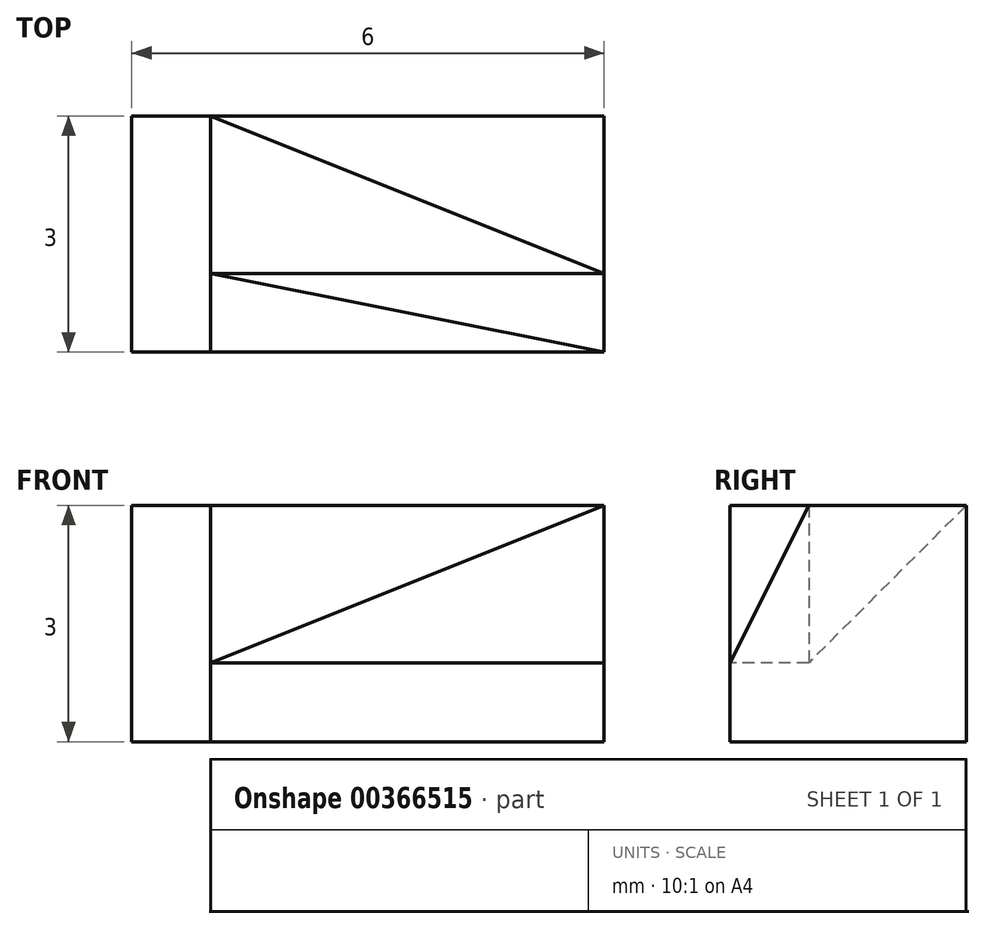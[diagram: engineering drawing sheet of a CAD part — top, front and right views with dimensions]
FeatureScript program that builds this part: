
annotation { "Feature Type Name" : "Feature", "Feature Type Description" : "" }
export const myFeature = defineFeature(function(context is Context, id is Id, definition is map)
    precondition{}
    {
        {
            var Q0;
            Q0=qCreatedBy(makeId("Top.planeOp"),FACE);
            var sketch = newSketch(context, id + "F0", { "sketchPlane" : qUnion([Q0])});
            skLineSegment(sketch, "E0", {"start": v(0, 0) * mm, "end": v(5, 0) * mm});
            skLineSegment(sketch, "E1", {"start": v(5, 0) * mm, "end": v(5, 3) * mm});
            skLineSegment(sketch, "E2", {"start": v(5, 3) * mm, "end": v(0, 3) * mm});
            skLineSegment(sketch, "E3", {"start": v(0, 3) * mm, "end": v(0, 0) * mm});
            skSolve(sketch);
        }
        {
            var Q0;
            Q0=qSketchRegion(id+"F0",true);
            extrude(context, id + "F1", {"entities" : qUnion([Q0]), "depth" : 3 * mm});
        }
        {
            var Q0;
            Q0=makeQuery(id+"F1.opExtrude","CAP_FACE",FACE,{"disambiguationData":[OSD([sQuery(id+"F0.wireOp",EDGE,"E0"),sQuery(id+"F0.wireOp",EDGE,"E1"),sQuery(id+"F0.wireOp",EDGE,"E2"),sQuery(id+"F0.wireOp",EDGE,"E3")])],"isStart":false});
            var sketch = newSketch(context, id + "F2", { "sketchPlane" : qUnion([Q0])});
            skLineSegment(sketch, "E4", {"start": v(0, 0) * mm, "end": v(0, 1) * mm});
            skLineSegment(sketch, "E5", {"start": v(0, 1) * mm, "end": v(5, 0) * mm});
            skSolve(sketch);
        }
        {
            var Q0;
            Q0=makeQuery(id+"F2.imprint","IMPRINT",FACE,{"disambiguationData":[TD([[makeQuery(id+"F2.imprint","IMPRINT",EDGE,{"derivedFrom":sQuery(id+"F2.wireOp",EDGE,"E4")}),1.0]])]});
            extrude(context, id + "F3", {"entities" : qUnion([Q0]), "operationType" : NewBodyOperationType.REMOVE, "oppositeDirection" : true, "depth" : 2 * mm});
        }
        {
            var Q0;
            Q0=makeQuery(id+"F1.opExtrude","SWEPT_FACE",FACE,{"disambiguationData":[OSD([sQuery(id+"F0.wireOp",EDGE,"E1")])]});
            var sketch = newSketch(context, id + "F4", { "sketchPlane" : qUnion([Q0])});
            skLineSegment(sketch, "E6", {"start": v(0, 0) * mm, "end": v(1, 0) * mm});
            skLineSegment(sketch, "E7", {"start": v(1, 0) * mm, "end": v(1, 3) * mm});
            skSolve(sketch);
        }
        {
            var Q0;
            Q0=sQuery(id+"F4.wireOp",VERTEX,"E7.end");
            var Q1;
            Q1=makeQuery(id+"F3.boolean.opBoolean","COPY",VERTEX,{"derivedFrom":makeQuery(id+"F3.opExtrude","CAP_VERTEX",VERTEX,{"disambiguationData":[OSD([sQuery(id+"F0.wireOp",EDGE,"E0"),sQuery(id+"F0.wireOp",EDGE,"E1"),sQuery(id+"F2.wireOp",EDGE,"E5")])],"isStart":false})});
            var Q2;
            Q2=makeQuery(id+"F3.boolean.opBoolean","COPY",VERTEX,{"derivedFrom":makeQuery(id+"F3.opExtrude","CAP_VERTEX",VERTEX,{"disambiguationData":[OSD([sQuery(id+"F0.wireOp",EDGE,"E3"),sQuery(id+"F2.wireOp",EDGE,"E4"),sQuery(id+"F2.wireOp",EDGE,"E5")])],"isStart":false})});
            cPlane(context, id + "F5", {"entities" : qUnion([Q0, Q1, Q2]), "cplaneType" : CPlaneType.THREE_POINT, "offset" : 25 * mm, "width" : 150 * mm, "height" : 150 * mm});
        }
        {
            var Q0;
            Q0=qCreatedBy(id+"F5.planeOp",FACE);
            var sketch = newSketch(context, id + "F6", { "sketchPlane" : qUnion([Q0])});
            skPoint(sketch, "E8.0", {"position": v(-0.08, 1.34) * mm});
            skPoint(sketch, "E9.0", {"position": v(5, 3.13) * mm});
            skPoint(sketch, "E10.0", {"position": v(5, 0.9) * mm});
            skLineSegment(sketch, "E11", {"start": v(-0.08, 1.34) * mm, "end": v(5, 0.9) * mm});
            skLineSegment(sketch, "E12", {"start": v(5, 3.13) * mm, "end": v(5, 0.9) * mm});
            skLineSegment(sketch, "E13", {"start": v(5, 3.13) * mm, "end": v(-0.08, 1.34) * mm});
            skLineSegment(sketch, "E14", {"start": v(5, 3.13) * mm, "end": v(6.74, 3.13) * mm});
            skLineSegment(sketch, "E15", {"start": v(6.74, 3.13) * mm, "end": v(6.74, 0.9) * mm});
            skLineSegment(sketch, "E16", {"start": v(6.74, 0.9) * mm, "end": v(5, 0.9) * mm});
            skSolve(sketch);
        }
        {
            var Q0;
            Q0=qSketchRegion(id+"F6",true);
            extrude(context, id + "F7", {"entities" : qUnion([Q0]), "operationType" : NewBodyOperationType.REMOVE, "depth" : 25 * mm});
        }
        {
            var Q0;
            Q0=makeQuery(id+"F1.opExtrude","CAP_VERTEX",VERTEX,{"disambiguationData":[OSD([sQuery(id+"F0.wireOp",EDGE,"E2"),sQuery(id+"F0.wireOp",EDGE,"E3")])],"isStart":false});
            var Q1;
            Q1=makeQuery(id+"F7.boolean.opBoolean","MERGE",VERTEX,{"derivedFrom":[makeQuery(id+"F3.boolean.opBoolean","COPY",VERTEX,{"derivedFrom":makeQuery(id+"F3.opExtrude","CAP_VERTEX",VERTEX,{"disambiguationData":[OSD([sQuery(id+"F0.wireOp",EDGE,"E3"),sQuery(id+"F2.wireOp",EDGE,"E4"),sQuery(id+"F2.wireOp",EDGE,"E5")])],"isStart":false})}),makeQuery(id+"F7.opExtrude","CAP_VERTEX",VERTEX,{"disambiguationData":[OSD([sQuery(id+"F6.wireOp",EDGE,"E11"),sQuery(id+"F6.wireOp",EDGE,"E13")])],"isStart":true})]});
            var Q2;
            Q2=sQuery(id+"F4.wireOp",VERTEX,"E7.end");
            cPlane(context, id + "F8", {"entities" : qUnion([Q0, Q1, Q2]), "cplaneType" : CPlaneType.THREE_POINT, "offset" : 25 * mm, "width" : 150 * mm, "height" : 150 * mm});
        }
        {
            var Q0;
            Q0=qCreatedBy(id+"F8.planeOp",FACE);
            var sketch = newSketch(context, id + "F9", { "sketchPlane" : qUnion([Q0])});
            skPoint(sketch, "E17.0", {"position": v(0, 4.24) * mm});
            skPoint(sketch, "E17.1", {"position": v(0, 1.41) * mm});
            skPoint(sketch, "E17.2", {"position": v(-5.2, 2.83) * mm});
            skLineSegment(sketch, "E18", {"start": v(0, 4.24) * mm, "end": v(0, 1.41) * mm});
            skLineSegment(sketch, "E19", {"start": v(-5.2, 2.83) * mm, "end": v(0, 4.24) * mm});
            skLineSegment(sketch, "E20", {"start": v(-5.2, 2.83) * mm, "end": v(0, 1.41) * mm});
            skLineSegment(sketch, "E21", {"start": v(-5.2, 2.83) * mm, "end": v(-5.2, 1.5) * mm});
            skLineSegment(sketch, "E22", {"start": v(-5.2, 1.5) * mm, "end": v(0, 1.41) * mm});
            skSolve(sketch);
        }
        {
            var Q0;
            Q0=qSketchRegion(id+"F9",true);
            extrude(context, id + "F10", {"entities" : qUnion([Q0]), "operationType" : NewBodyOperationType.REMOVE, "oppositeDirection" : true, "depth" : 25 * mm});
        }
        {
            var Q0;
            Q0=qCreatedBy(makeId("Front.planeOp"),FACE);
            var sketch = newSketch(context, id + "F11", { "sketchPlane" : qUnion([Q0])});
            skLineSegment(sketch, "E23", {"start": v(0, 0) * mm, "end": v(-1, 0) * mm});
            skLineSegment(sketch, "E24", {"start": v(-1, 0) * mm, "end": v(-1, 3) * mm});
            skLineSegment(sketch, "E25", {"start": v(-1, 3) * mm, "end": v(0, 3) * mm});
            skLineSegment(sketch, "E26", {"start": v(0, 3) * mm, "end": v(0, 0) * mm});
            skSolve(sketch);
        }
        {
            var Q0;
            Q0=qSketchRegion(id+"F11",true);
            extrude(context, id + "F12", {"entities" : qUnion([Q0]), "oppositeDirection" : true, "depth" : 3 * mm});
        }
    });
